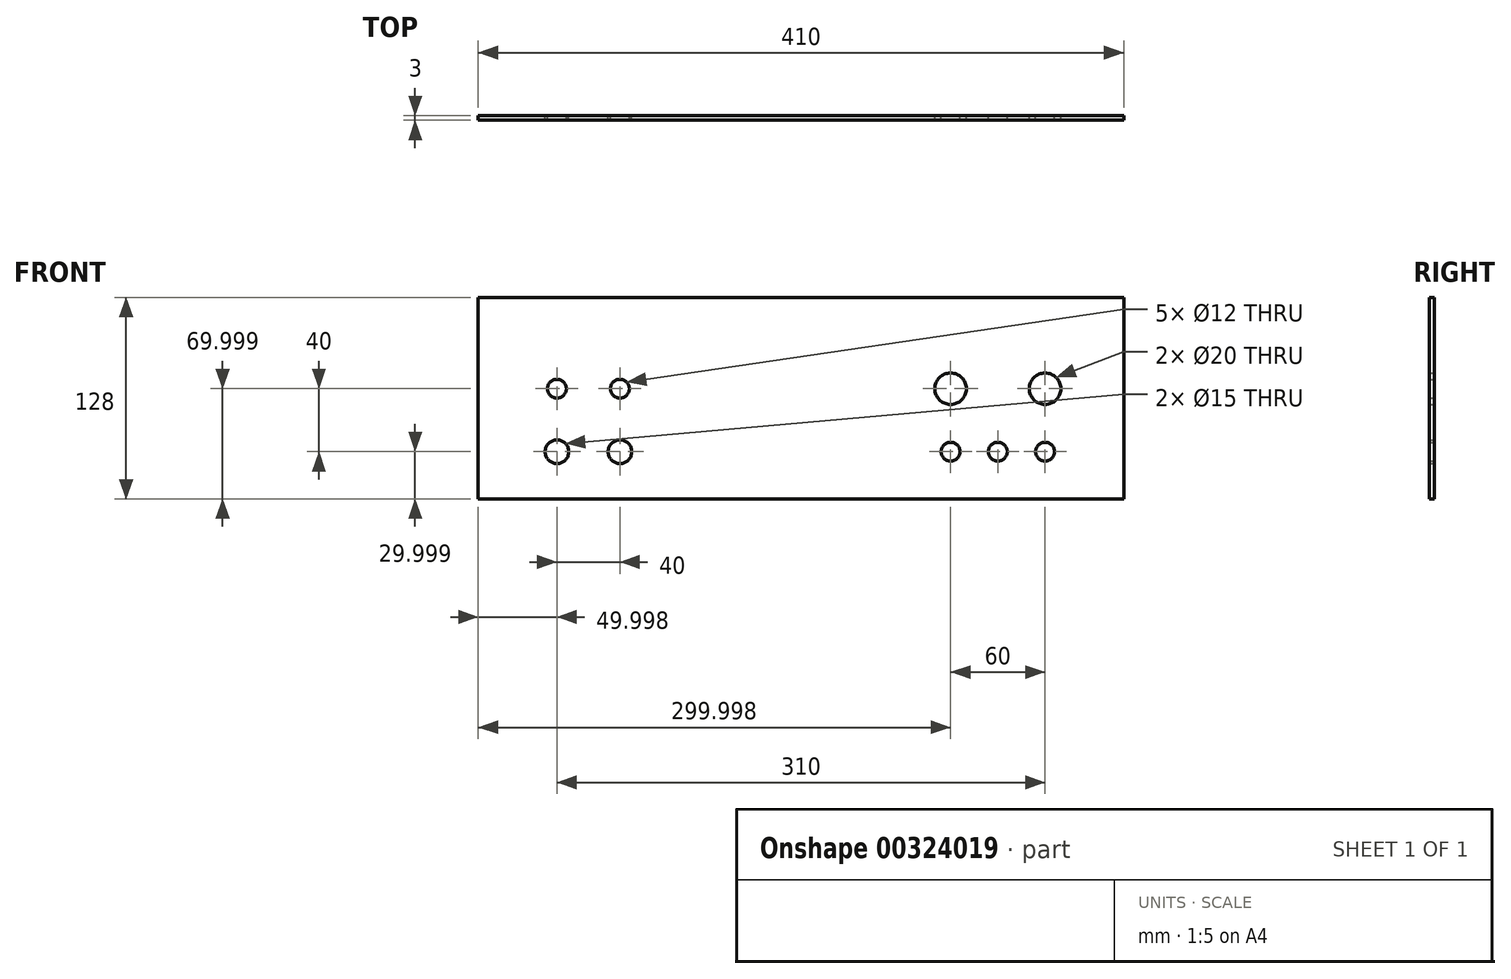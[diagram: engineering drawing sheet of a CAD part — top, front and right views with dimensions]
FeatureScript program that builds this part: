
annotation { "Feature Type Name" : "Feature", "Feature Type Description" : "" }
export const myFeature = defineFeature(function(context is Context, id is Id, definition is map)
    precondition{}
    {
        {
            var Q0;
            Q0=qCreatedBy(makeId("Front.planeOp"),FACE);
            var sketch = newSketch(context, id + "F0", { "sketchPlane" : qUnion([Q0])});
            skLineSegment(sketch, "E0.bottom", {"start": v(-422.38, 243.79) * mm, "end": v(-12.38, 243.79) * mm});
            skLineSegment(sketch, "E0.top", {"start": v(-422.38, 115.79) * mm, "end": v(-12.38, 115.79) * mm});
            skLineSegment(sketch, "E0.left", {"start": v(-422.38, 243.79) * mm, "end": v(-422.38, 115.79) * mm});
            skLineSegment(sketch, "E0.right", {"start": v(-12.38, 243.79) * mm, "end": v(-12.38, 115.79) * mm});
            skPoint(sketch, "E1", {"position": v(-332.38, 185.79) * mm});
            skPoint(sketch, "E2", {"position": v(-372.38, 185.79) * mm});
            skPoint(sketch, "E3", {"position": v(-372.38, 145.79) * mm});
            skPoint(sketch, "E4", {"position": v(-332.38, 145.79) * mm});
            skPoint(sketch, "E5", {"position": v(-62.38, 185.79) * mm});
            skCircle(sketch, "E6", {"center": v(-372.38, 145.79) * mm, "radius": 7.5 * mm});
            skCircle(sketch, "E7", {"center": v(-332.38, 145.79) * mm, "radius": 7.5 * mm});
            skCircle(sketch, "E8", {"center": v(-332.38, 185.79) * mm, "radius": 6 * mm});
            skCircle(sketch, "E9", {"center": v(-372.38, 185.79) * mm, "radius": 6 * mm});
            skCircle(sketch, "E10", {"center": v(-122.38, 185.79) * mm, "radius": 10 * mm});
            skCircle(sketch, "E11", {"center": v(-62.38, 185.79) * mm, "radius": 10 * mm});
            skLineSegment(sketch, "E12", {"start": v(-217.38, 243.79) * mm, "end": v(-217.38, 115.79) * mm});
            skCircle(sketch, "E13", {"center": v(-62.38, 145.79) * mm, "radius": 6 * mm});
            skCircle(sketch, "E14", {"center": v(-92.38, 145.79) * mm, "radius": 6 * mm});
            skCircle(sketch, "E15", {"center": v(-122.38, 145.79) * mm, "radius": 6 * mm});
            skLineSegment(sketch, "E16", {"start": v(-372.38, 185.79) * mm, "end": v(-332.38, 185.79) * mm, "construction": true});
            skLineSegment(sketch, "E17", {"start": v(-372.38, 145.79) * mm, "end": v(-332.38, 145.79) * mm, "construction": true});
            skLineSegment(sketch, "E18", {"start": v(-352.38, 185.79) * mm, "end": v(-352.38, 145.79) * mm, "construction": true});
            skLineSegment(sketch, "E19", {"start": v(-372.38, 145.79) * mm, "end": v(-422.38, 145.79) * mm, "construction": true});
            skLineSegment(sketch, "E20", {"start": v(-62.38, 145.79) * mm, "end": v(-12.38, 145.79) * mm, "construction": true});
            skLineSegment(sketch, "E21", {"start": v(-332.38, 145.79) * mm, "end": v(-332.38, 115.79) * mm, "construction": true});
            skLineSegment(sketch, "E22", {"start": v(-62.38, 145.79) * mm, "end": v(-62.38, 115.79) * mm, "construction": true});
            skLineSegment(sketch, "E23", {"start": v(-122.38, 145.79) * mm, "end": v(-92.38, 145.79) * mm, "construction": true});
            skLineSegment(sketch, "E24", {"start": v(-62.38, 145.79) * mm, "end": v(-92.38, 145.79) * mm, "construction": true});
            skLineSegment(sketch, "E25", {"start": v(-62.38, 185.79) * mm, "end": v(-122.38, 185.79) * mm, "construction": true});
            skLineSegment(sketch, "E26", {"start": v(-92.38, 145.79) * mm, "end": v(-92.38, 185.79) * mm, "construction": true});
            skSolve(sketch);
        }
        {
            var Q0;
            Q0 = qSketchRegion(id + "F0", true);
            extrude(context, id + "F1", {"entities" : qUnion([Q0]), "depth" : 3 * mm});
        }
    });
